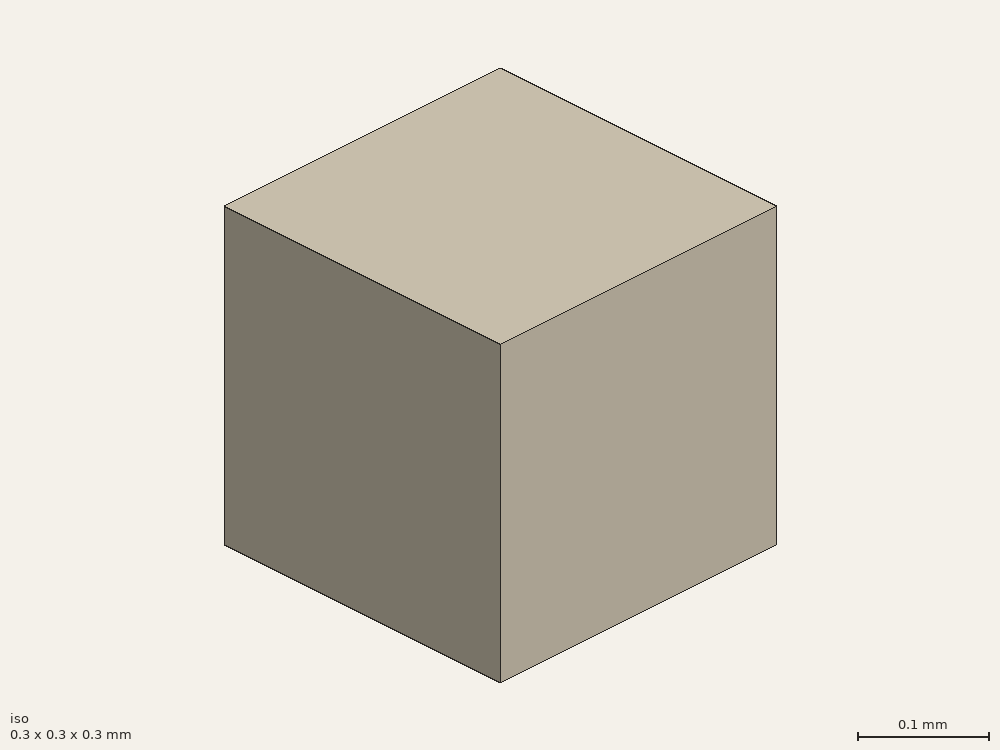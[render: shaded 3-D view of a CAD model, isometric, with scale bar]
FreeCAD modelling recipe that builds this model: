
FCSTD DOCUMENT  (FreeCAD 0.21R33694 (Git))
Label: square-planar
License: All rights reserved
LicenseURL: http://en.wikipedia.org/wiki/All_rights_reserved
objects: Part::Part2DObjectPython×18, App::FeaturePython×9, Part::Extrusion×8, Part::Cut×6, Part::FeaturePython×2
note: 34 computed .brp shape members not serialized (recipe doc carries the construction recipe); baked Part::Feature solids carry a one-line shape summary decoded from their .brp

FEATURE [Part::Part2DObjectPython] Rectangle  label="gp2D"  # Draft 2D object (typed FeaturePython)
  Area = 22500
  ChamferSize = 0
  Columns = 1
  FilletRadius = 0
  Height = 150
  Length = 150
  MakeFace = true
  Placement = pos=(-75,-75,0) rot=(0,0,1;0rad)
  Rows = 1
FEATURE [Part::Part2DObjectPython] Polygon  label="inner2D"  # Draft 2D object (typed FeaturePython)
  Area = 1.10213
  ChamferSize = 0
  DrawMode = 0
  FacesNumber = 16
  FilletRadius = 0
  MakeFace = true
  Radius = 0.6
FEATURE [Part::Part2DObjectPython] Polygon001  label="outer2D"  # Draft 2D object (typed FeaturePython)
  Area = 13.1181
  ChamferSize = 0
  DrawMode = 0
  FacesNumber = 16
  FilletRadius = 0
  MakeFace = true
  Radius = 2.07
FEATURE [Part::Part2DObjectPython] Polygon002  label="barrel2D"  # Draft 2D object (typed FeaturePython)
  Area = 27.5532
  ChamferSize = 0
  DrawMode = 0
  FacesNumber = 16
  FilletRadius = 0
  MakeFace = true
  Radius = 3
FEATURE [Part::Part2DObjectPython] Clone2D  label="inner2D (2D)"  # Draft 2D object (typed FeaturePython)
  Fuse = false
  Objects = -> [Polygon]
  Scale = (1,1,1)
FEATURE [Part::Extrusion] Extrude001  label="coax-pin"
  Base = -> Clone2D
  Dir = (0,0,1)
  DirMode = 2
  FaceMakerClass = Part::FaceMakerBullseye
  LengthFwd = -19
  LengthRev = 0
  Solid = false
  Symmetric = false
FEATURE [Part::Extrusion] Extrude002  label="coax-dielectic"
  Base = -> Polygon001
  Dir = (0,0,1)
  DirMode = 2
  FaceMakerClass = Part::FaceMakerBullseye
  LengthFwd = -19
  LengthRev = 0
  Solid = false
  Symmetric = false
FEATURE [Part::Extrusion] Extrude003  label="coax-outer"
  Base = -> Polygon002
  Dir = (0,0,1)
  DirMode = 2
  FaceMakerClass = Part::FaceMakerBullseye
  LengthFwd = -20
  LengthRev = 0
  Solid = false
  Symmetric = false
FEATURE [Part::Cut] Cut001  label="teflon"
  Base = -> Extrude002
  Tool = -> Extrude001
FEATURE [Part::Extrusion] Extrude004
  Base = -> Rectangle
  Dir = (0,0,1)
  DirMode = 2
  FaceMakerClass = Part::FaceMakerBullseye
  LengthFwd = -0.2
  LengthRev = 0
  Solid = false
  Symmetric = false
FEATURE [Part::Part2DObjectPython] Clone2D001  label="barrel2D (2D)"  # Draft 2D object (typed FeaturePython)
  Fuse = false
  Objects = -> [Polygon002]
  Scale = (1,1,1)
FEATURE [Part::Extrusion] Extrude005
  Base = -> Clone2D001
  Dir = (0,0,1)
  DirMode = 2
  FaceMakerClass = Part::FaceMakerBullseye
  LengthFwd = -5
  LengthRev = 0
  Solid = false
  Symmetric = false
FEATURE [Part::Part2DObjectPython] Rectangle003  label="air2D"  # Draft 2D object (typed FeaturePython)
  Area = 90000
  ChamferSize = 0
  Columns = 1
  FilletRadius = 0
  Height = 300
  Length = 300
  MakeFace = true
  Placement = pos=(-150,-150,0) rot=(0,0,1;0rad)
  Rows = 1
FEATURE [Part::Part2DObjectPython] Wire  label="_Pport"  # Draft 2D object (typed FeaturePython)
  Area = 1.31181e-05
  ChamferSize = 0
  Closed = true
  End = (3e-16,-0.00207,-0.019)
  FilletRadius = 0
  Length = 0.0129228
  MakeFace = true
  Placement = pos=(0.000792155,-0.00191243,-0.019) rot=(0,0,1;0rad)
  Points = (16) [(0,0,0),(0.000671556,0.00044872,0),(0.00112028,0.00112028,0),(0.00127785,0.00191243,0),(0.00112028,0.00270459,0),(0.000671556,0.00337614,0),+10 more]
  Start = (0.000792155,-0.00191243,-0.019)
  Subdivisions = 0
FEATURE [Part::Part2DObjectPython] Wire001  label="_Pi"  # Draft 2D object (typed FeaturePython)
  Area = 1.10213e-06
  ChamferSize = 0
  Closed = true
  End = (0.00022961,-0.000554328,-0.019)
  FilletRadius = 0
  Length = 0.00374573
  MakeFace = true
  Placement = pos=(0.000424264,-0.000424264,-0.019) rot=(0,0,1;0rad)
  Points = (16) [(0,0,0),(0.000130064,0.000194654,0),(0.000175736,0.000424264,0),(0.000130064,0.000653874,0),(0,0.000848528,0),(-0.000194654,0.000978592,0),+10 more]
  Start = (0.000424264,-0.000424264,-0.019)
  Subdivisions = 0
FEATURE [Part::Part2DObjectPython] Line  label="_Pv"  # Draft 2D object (typed FeaturePython)
  Area = 0
  ChamferSize = 0
  Closed = false
  End = (0.000424264,-0.000424264,-0.019)
  FilletRadius = 0
  Length = 0.00147
  MakeFace = true
  Placement = pos=(0.00146371,-0.00146371,-0.019) rot=(0,0,1;0rad)
  Points = (2) [(0,0,0),(-0.00103945,0.00103945,0)]
  Start = (0.00146371,-0.00146371,-0.019)
  Subdivisions = 0
FEATURE [App::FeaturePython] Text  label="_Btop(radiation){top}"  # WARN: FeaturePython — macro-defined, semantics opaque (R4)
  Placement = pos=(0.308621,-0.303467,0.3) rot=(0,0,1;0rad)
  Text = .
FEATURE [App::FeaturePython] Text001  label="_Bfront(radiation){front}"  # WARN: FeaturePython — macro-defined, semantics opaque (R4)
  Placement = pos=(0.308621,-0.303467,0.3) rot=(0,0,1;0rad)
  Text = .
FEATURE [App::FeaturePython] Text002  label="_Bright(radiation){right}"  # WARN: FeaturePython — macro-defined, semantics opaque (R4)
  Placement = pos=(0.308621,-0.303467,0.3) rot=(0,0,1;0rad)
  Text = .
FEATURE [App::FeaturePython] Text003  label="_Bleft(radiation){left}"  # WARN: FeaturePython — macro-defined, semantics opaque (R4)
  Placement = pos=(0.308621,-0.303467,0.3) rot=(0,0,1;0rad)
  Text = .
FEATURE [App::FeaturePython] Text004  label="_Bback(radiation){back}"  # WARN: FeaturePython — macro-defined, semantics opaque (R4)
  Placement = pos=(0.308621,-0.303467,0.3) rot=(0,0,1;0rad)
  Text = .
FEATURE [App::FeaturePython] Text005  label="_Bbottom(radiation){bottom}"  # WARN: FeaturePython — macro-defined, semantics opaque (R4)
  Placement = pos=(0.308621,-0.303467,0.3) rot=(0,0,1;0rad)
  Text = .
FEATURE [App::FeaturePython] Text006  label="_Sin(PV){port}"  # WARN: FeaturePython — macro-defined, semantics opaque (R4)
  Placement = pos=(0.308621,-0.303467,0.3) rot=(0,0,1;0rad)
  Text = .
FEATURE [App::FeaturePython] Text007  label="_Lin(1,voltage){v}"  # WARN: FeaturePython — macro-defined, semantics opaque (R4)
  Placement = pos=(0.308621,-0.303467,0.3) rot=(0,0,1;0rad)
  Text = .
FEATURE [App::FeaturePython] Text008  label="_Lin(1,current){i}"  # WARN: FeaturePython — macro-defined, semantics opaque (R4)
  Placement = pos=(0.308621,-0.303467,0.3) rot=(0,0,1;0rad)
  Text = .
FEATURE [Part::Cut] Cut002  label="gp"
  Base = -> Extrude004
  Tool = -> Extrude005
FEATURE [Part::Part2DObjectPython] Rectangle010  label="antenna2D"  # Draft 2D object (typed FeaturePython)
  Area = 1600
  ChamferSize = 0
  Columns = 1
  FilletRadius = 0
  Height = 40
  Length = 40
  MakeFace = true
  Placement = pos=(-20,0,4.5) rot=(1,0,0;1.5708rad)
  Rows = 1
FEATURE [Part::Part2DObjectPython] Rectangle013  # Draft 2D object (typed FeaturePython)
  Area = 5
  ChamferSize = 0
  Columns = 1
  FilletRadius = 0
  Height = 2.5
  Length = 2
  MakeFace = true
  Placement = pos=(-1,0,0) rot=(1,0,0;1.5708rad)
  Rows = 1
FEATURE [Part::Extrusion] Extrude009  label="antenna"
  Base = -> Rectangle010
  Dir = (0,-1,2e-16)
  DirMode = 2
  FaceMakerClass = Part::FaceMakerBullseye
  LengthFwd = 0.2
  LengthRev = 0
  Placement = pos=(0,0.1,-2) rot=(0,0,1;0rad)
  Solid = false
  Symmetric = false
FEATURE [Part::Extrusion] Extrude  label="air"
  Base = -> Rectangle003
  Dir = (0,0,1)
  DirMode = 2
  FaceMakerClass = Part::FaceMakerBullseye
  LengthFwd = 300
  LengthRev = 0
  Placement = pos=(0,0,-110) rot=(0,0,1;0rad)
  Solid = false
  Symmetric = false
FEATURE [Part::Cut] Cut
  Base = -> Extrude
  Tool = -> Cut002
FEATURE [Part::Cut] Cut003
  Base = -> Cut
  Tool = -> Extrude003
FEATURE [Part::Extrusion] Extrude010  label="feed"
  Base = -> Rectangle013
  Dir = (0,-1,2e-16)
  DirMode = 2
  FaceMakerClass = Part::FaceMakerBullseye
  LengthFwd = 0.2
  LengthRev = 0
  Placement = pos=(0,0.1,0) rot=(0,0,1;0rad)
  Solid = false
  Symmetric = false
FEATURE [Part::Cut] Cut004
  Base = -> Cut003
  Tool = -> Extrude010
FEATURE [Part::Cut] Cut005
  Base = -> Cut004
  Tool = -> Extrude009
FEATURE [Part::FeaturePython] BooleanFragments  # WARN: FeaturePython — macro-defined, semantics opaque (R4)
  Mode = 0
  Objects = -> [Cut005,Cut001]
  Tolerance = 0
FEATURE [Part::FeaturePython] Clone  label="scaled"  # Draft clone (typed FeaturePython)
  AttacherType = Attacher::AttachEngine3D
  Fuse = false
  Objects = -> [BooleanFragments]
  Scale = (0.001,0.001,0.001)
FEATURE [Part::Part2DObjectPython] Rectangle014  label="_Pfront"  # Draft 2D object (typed FeaturePython)
  Area = 0.09
  ChamferSize = 0
  Columns = 1
  FilletRadius = 0
  Height = 0.3
  Length = 0.3
  MakeFace = true
  Placement = pos=(-0.15,-0.15,-0.11) rot=(1,0,0;1.5708rad)
  Rows = 1
FEATURE [Part::Part2DObjectPython] Rectangle015  label="_Pback"  # Draft 2D object (typed FeaturePython)
  Area = 0.09
  ChamferSize = 0
  Columns = 1
  FilletRadius = 0
  Height = 0.3
  Length = 0.3
  MakeFace = true
  Placement = pos=(-0.15,0.15,-0.11) rot=(1,0,0;1.5708rad)
  Rows = 1
FEATURE [Part::Part2DObjectPython] Rectangle016  label="_Ptop"  # Draft 2D object (typed FeaturePython)
  Area = 0.09
  ChamferSize = 0
  Columns = 1
  FilletRadius = 0
  Height = 0.3
  Length = 0.3
  MakeFace = true
  Placement = pos=(-0.15,-0.15,0.19) rot=(0,0,1;0rad)
  Rows = 1
FEATURE [Part::Part2DObjectPython] Rectangle017  label="_Pbottom"  # Draft 2D object (typed FeaturePython)
  Area = 0.09
  ChamferSize = 0
  Columns = 1
  FilletRadius = 0
  Height = 0.3
  Length = 0.3
  MakeFace = true
  Placement = pos=(-0.15,-0.15,-0.11) rot=(0,0,1;0rad)
  Rows = 1
FEATURE [Part::Part2DObjectPython] Rectangle018  label="_Pright"  # Draft 2D object (typed FeaturePython)
  Area = 0.09
  ChamferSize = 0
  Columns = 1
  FilletRadius = 0
  Height = 0.3
  Length = 0.3
  MakeFace = true
  Placement = pos=(0.15,-0.15,-0.11) rot=(0.57735,0.57735,0.57735;2.0944rad)
  Rows = 1
FEATURE [Part::Part2DObjectPython] Rectangle019  label="_Pleft"  # Draft 2D object (typed FeaturePython)
  Area = 0.09
  ChamferSize = 0
  Columns = 1
  FilletRadius = 0
  Height = 0.3
  Length = 0.3
  MakeFace = true
  Placement = pos=(-0.15,-0.15,-0.11) rot=(0.57735,0.57735,0.57735;2.0944rad)
  Rows = 1
